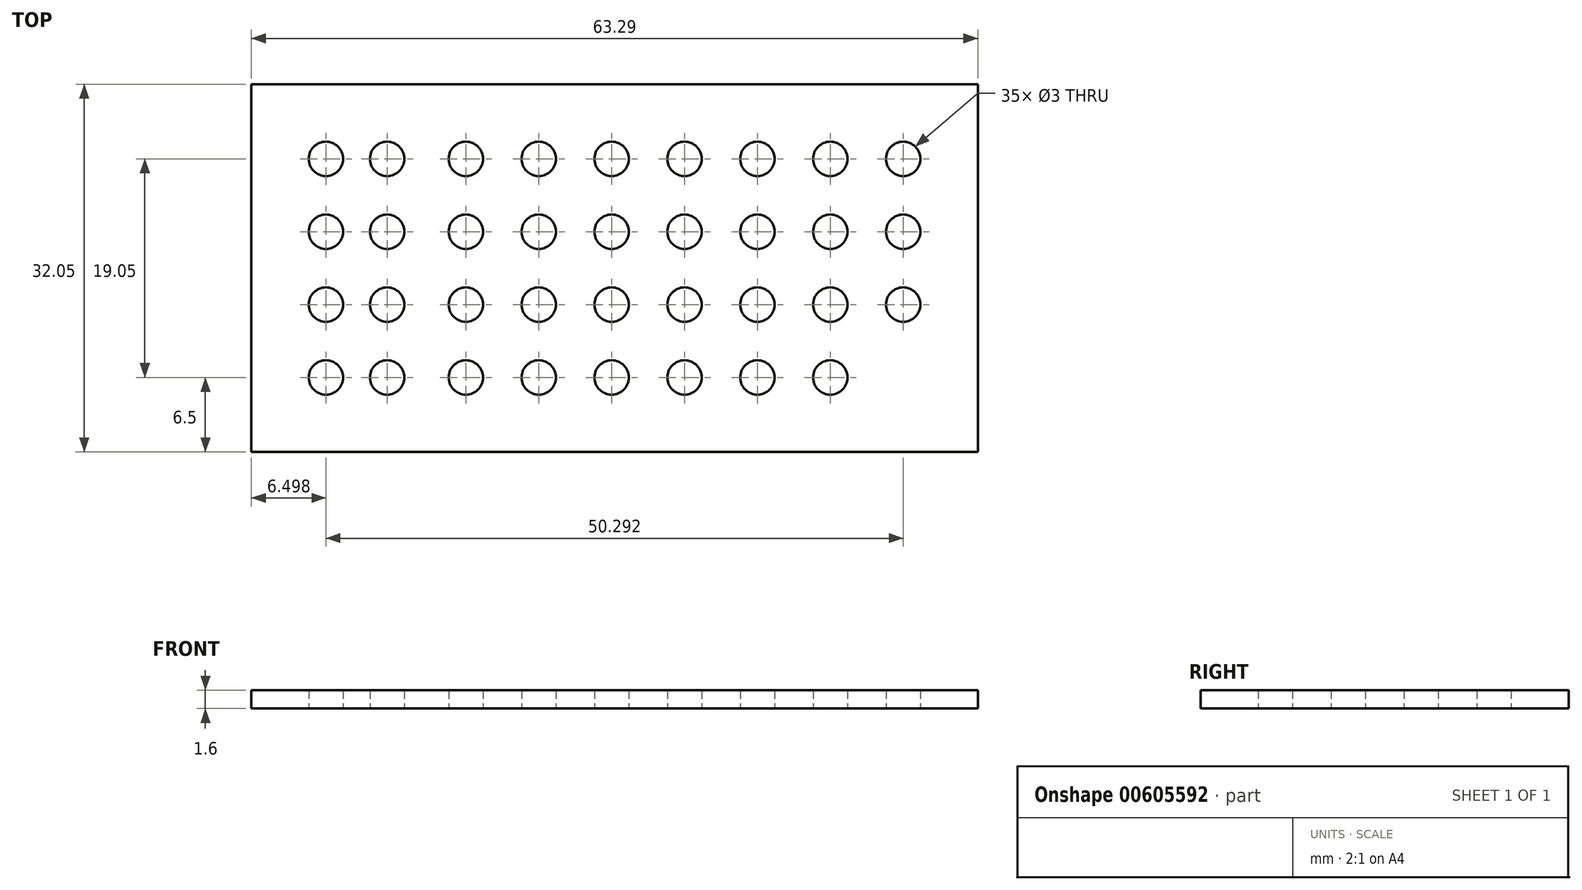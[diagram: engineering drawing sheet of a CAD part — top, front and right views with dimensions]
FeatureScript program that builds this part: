
annotation { "Feature Type Name" : "Feature", "Feature Type Description" : "" }
export const myFeature = defineFeature(function(context is Context, id is Id, definition is map)
    precondition{}
    {
        {
            var Q0;
            Q0=qCreatedBy(makeId("Top.planeOp"),FACE);
            var sketch = newSketch(context, id + "F0", { "sketchPlane" : qUnion([Q0])});
            skCircle(sketch, "E0", {"center": v(0, 0) * mm, "radius": 1.5 * mm});
            skCircle(sketch, "E1.0.1.0", {"center": v(0, 6.35) * mm, "radius": 1.5 * mm});
            skCircle(sketch, "E1.0.2.0", {"center": v(0, 12.7) * mm, "radius": 1.5 * mm});
            skCircle(sketch, "E1.0.3.0", {"center": v(0, 19.05) * mm, "radius": 1.5 * mm});
            skCircle(sketch, "E1.1.0.0", {"center": v(6.35, 0) * mm, "radius": 1.5 * mm});
            skCircle(sketch, "E1.1.1.0", {"center": v(6.35, 6.35) * mm, "radius": 1.5 * mm});
            skCircle(sketch, "E1.1.2.0", {"center": v(6.35, 12.7) * mm, "radius": 1.5 * mm});
            skCircle(sketch, "E1.1.3.0", {"center": v(6.35, 19.05) * mm, "radius": 1.5 * mm});
            skCircle(sketch, "E1.2.0.0", {"center": v(12.7, 0) * mm, "radius": 1.5 * mm});
            skCircle(sketch, "E1.2.1.0", {"center": v(12.7, 6.35) * mm, "radius": 1.5 * mm});
            skCircle(sketch, "E1.2.2.0", {"center": v(12.7, 12.7) * mm, "radius": 1.5 * mm});
            skCircle(sketch, "E1.2.3.0", {"center": v(12.7, 19.05) * mm, "radius": 1.5 * mm});
            skCircle(sketch, "E1.3.0.0", {"center": v(19.05, 0) * mm, "radius": 1.5 * mm});
            skCircle(sketch, "E1.3.1.0", {"center": v(19.05, 6.35) * mm, "radius": 1.5 * mm});
            skCircle(sketch, "E1.3.2.0", {"center": v(19.05, 12.7) * mm, "radius": 1.5 * mm});
            skCircle(sketch, "E1.3.3.0", {"center": v(19.05, 19.05) * mm, "radius": 1.5 * mm});
            skCircle(sketch, "E1.4.0.0", {"center": v(25.4, 0) * mm, "radius": 1.5 * mm});
            skCircle(sketch, "E1.4.1.0", {"center": v(25.4, 6.35) * mm, "radius": 1.5 * mm});
            skCircle(sketch, "E1.4.2.0", {"center": v(25.4, 12.7) * mm, "radius": 1.5 * mm});
            skCircle(sketch, "E1.4.3.0", {"center": v(25.4, 19.05) * mm, "radius": 1.5 * mm});
            skCircle(sketch, "E1.5.0.0", {"center": v(31.75, 0) * mm, "radius": 1.5 * mm});
            skCircle(sketch, "E1.5.1.0", {"center": v(31.75, 6.35) * mm, "radius": 1.5 * mm});
            skCircle(sketch, "E1.5.2.0", {"center": v(31.75, 12.7) * mm, "radius": 1.5 * mm});
            skCircle(sketch, "E1.5.3.0", {"center": v(31.75, 19.05) * mm, "radius": 1.5 * mm});
            skCircle(sketch, "E1.6.1.0", {"center": v(38.1, 6.35) * mm, "radius": 1.5 * mm});
            skCircle(sketch, "E1.6.2.0", {"center": v(38.1, 12.7) * mm, "radius": 1.5 * mm});
            skCircle(sketch, "E1.6.3.0", {"center": v(38.1, 19.05) * mm, "radius": 1.5 * mm});
            skLineSegment(sketch, "E1.direction1", {"start": v(0, 0) * mm, "end": v(6.35, 0) * mm, "construction": true});
            skLineSegment(sketch, "E1.direction2", {"start": v(0, 0) * mm, "end": v(0, 6.35) * mm, "construction": true});
            skCircle(sketch, "E2.1.0.0", {"center": v(-6.86, 0) * mm, "radius": 1.5 * mm});
            skCircle(sketch, "E2.1.1.0", {"center": v(-6.86, 6.35) * mm, "radius": 1.5 * mm});
            skCircle(sketch, "E2.1.2.0", {"center": v(-6.86, 12.7) * mm, "radius": 1.5 * mm});
            skCircle(sketch, "E2.1.3.0", {"center": v(-6.86, 19.05) * mm, "radius": 1.5 * mm});
            skLineSegment(sketch, "E2.direction1", {"start": v(0, 0) * mm, "end": v(-6.86, 0) * mm, "construction": true});
            skCircle(sketch, "E3.1.0.0", {"center": v(-12.2, 12.7) * mm, "radius": 1.5 * mm});
            skCircle(sketch, "E3.1.0.1", {"center": v(-12.2, 19.05) * mm, "radius": 1.5 * mm});
            skCircle(sketch, "E3.1.0.2", {"center": v(-12.2, 0) * mm, "radius": 1.5 * mm});
            skCircle(sketch, "E3.1.0.3", {"center": v(-12.2, 6.35) * mm, "radius": 1.5 * mm});
            skLineSegment(sketch, "E3.direction1", {"start": v(-6.86, 0) * mm, "end": v(-12.2, 0) * mm, "construction": true});
            skLineSegment(sketch, "E4.bottom", {"start": v(-18.7, 25.55) * mm, "end": v(44.6, 25.55) * mm});
            skLineSegment(sketch, "E4.top", {"start": v(-18.7, -6.5) * mm, "end": v(44.6, -6.5) * mm});
            skLineSegment(sketch, "E4.left", {"start": v(-18.7, 25.55) * mm, "end": v(-18.7, -6.5) * mm});
            skLineSegment(sketch, "E4.right", {"start": v(44.6, 25.55) * mm, "end": v(44.6, -6.5) * mm});
            skLineSegment(sketch, "E5.bottom", {"start": v(12.7, 12.7) * mm, "end": v(12.7, 12.7) * mm});
            skLineSegment(sketch, "E5.top", {"start": v(12.7, 6.35) * mm, "end": v(12.7, 6.35) * mm});
            skLineSegment(sketch, "E5.left", {"start": v(12.7, 12.7) * mm, "end": v(12.7, 6.35) * mm, "construction": true});
            skLineSegment(sketch, "E5.right", {"start": v(12.7, 12.7) * mm, "end": v(12.7, 6.35) * mm, "construction": true});
            skLineSegment(sketch, "E6", {"start": v(12.7, 9.52) * mm, "end": v(44.6, 9.52) * mm, "construction": true});
            skSolve(sketch);
        }
        {
            var Q0;
            Q0 = qSketchRegion(id + "F0", true);
            extrude(context, id + "F1", {"entities" : qUnion([Q0]), "depth" : 1.6 * mm, "offsetDistance" : 25 * mm});
        }
    });
